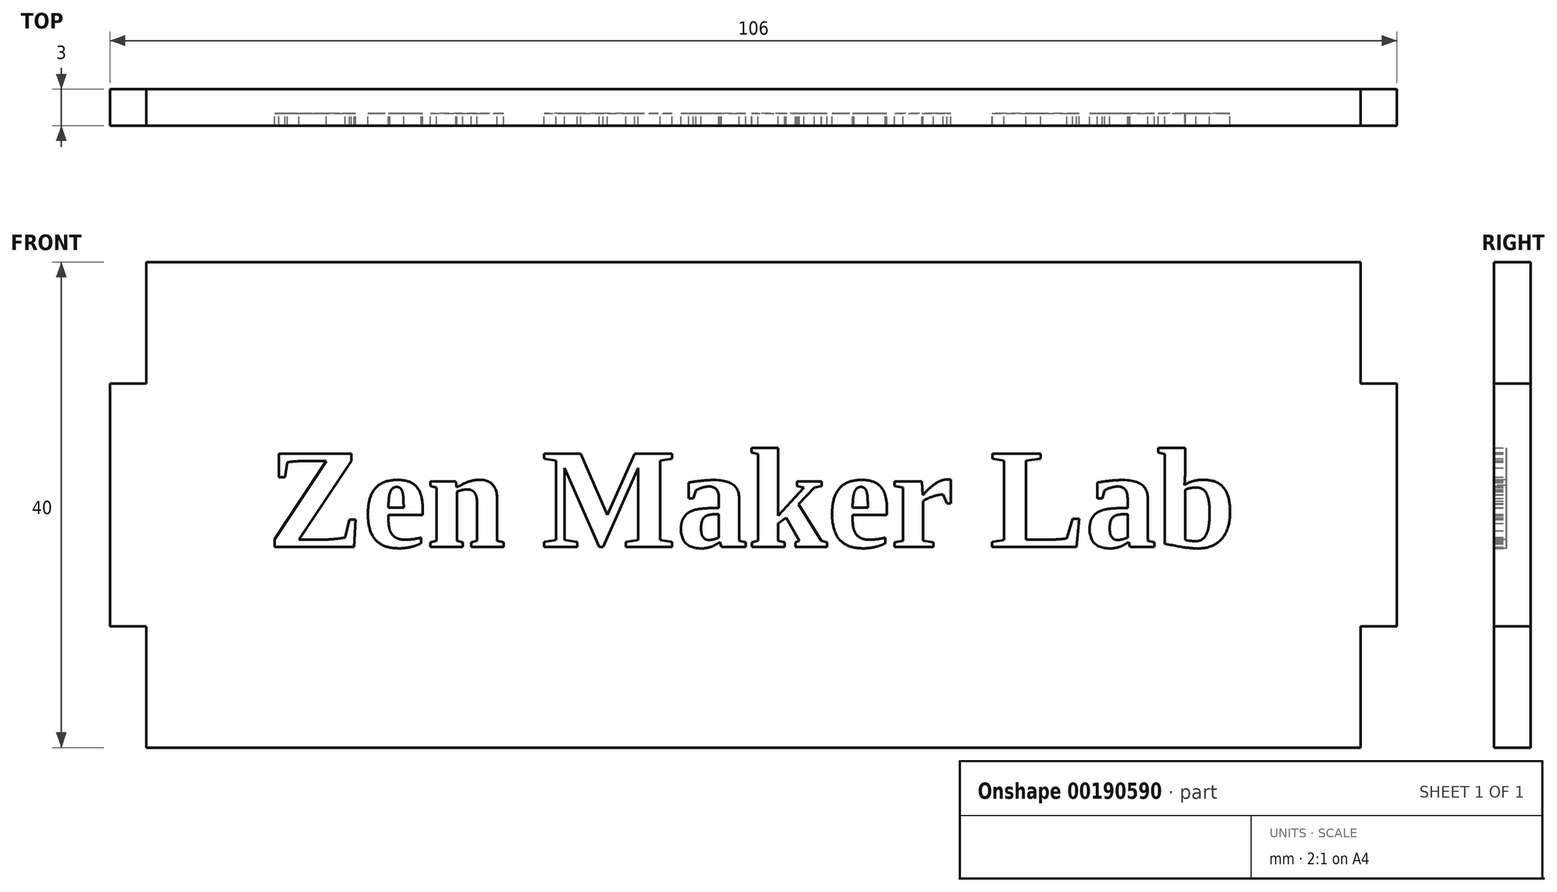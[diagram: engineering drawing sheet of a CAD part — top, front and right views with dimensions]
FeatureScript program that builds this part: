
annotation { "Feature Type Name" : "Feature", "Feature Type Description" : "" }
export const myFeature = defineFeature(function(context is Context, id is Id, definition is map)
    precondition{}
    {
        {
            var Q0;
            Q0=qCreatedBy(makeId("Front.planeOp"),FACE);
            var sketch = newSketch(context, id + "F0", { "sketchPlane" : qUnion([Q0])});
            skLineSegment(sketch, "E0.bottom", {"start": v(50, 20) * mm, "end": v(-50, 20) * mm});
            skLineSegment(sketch, "E0.top", {"start": v(50, -20) * mm, "end": v(-50, -20) * mm});
            skLineSegment(sketch, "E0.left", {"start": v(50, 20) * mm, "end": v(50, 10) * mm});
            skLineSegment(sketch, "E0.right", {"start": v(-50, 20) * mm, "end": v(-50, 10) * mm});
            skPoint(sketch, "E0.middle", {"position": v(0, 0) * mm});
            skLineSegment(sketch, "E1.bottom", {"start": v(50, 10) * mm, "end": v(53, 10) * mm});
            skLineSegment(sketch, "E1.top", {"start": v(50, -10) * mm, "end": v(53, -10) * mm});
            skLineSegment(sketch, "E1.right", {"start": v(53, 10) * mm, "end": v(53, -10) * mm});
            skLineSegment(sketch, "E2", {"start": v(0, 20) * mm, "end": v(0, -20) * mm, "construction": true});
            skLineSegment(sketch, "E3.MirrorCS", {"start": v(-50, 10) * mm, "end": v(-50, 10) * mm});
            skLineSegment(sketch, "E4.MirrorCS", {"start": v(-50, -10) * mm, "end": v(-53, -10) * mm});
            skLineSegment(sketch, "E5.MirrorCS", {"start": v(-50, 10) * mm, "end": v(-53, 10) * mm});
            skLineSegment(sketch, "E6.MirrorCS", {"start": v(-53, 10) * mm, "end": v(-53, -10) * mm});
            skLineSegment(sketch, "E7", {"start": v(-50, -10) * mm, "end": v(-50, -20) * mm});
            skLineSegment(sketch, "E8", {"start": v(50, -10) * mm, "end": v(50, -20) * mm});
            skText(sketch, "E9", { "text": "Zen Maker Lab", "fontName": "Tinos-Bold.ttf"});
            const initialGuessF0  = {"E9": [-0.04, -0.00347, 1, 0, 0.00847]};
            skSetInitialGuess(sketch, initialGuessF0);
            skSolve(sketch);
        }
        {
            var Q0;
            Q0=makeQuery(id+"F0.imprint","IMPRINT",FACE,{"disambiguationData":[TD([[makeQuery(id+"F0.imprint","IMPRINT",EDGE,{"derivedFrom":sQuery(id+"F0.wireOp",EDGE,"E0.bottom")}),1.0]])]});
            var Q1;
            Q1=makeQuery(id+"F0.imprint","IMPRINT",FACE,{"disambiguationData":[TD([[makeQuery(id+"F0.imprint","IMPRINT",EDGE,{"derivedFrom":sQuery(id+"F0.wireOp",EDGE,"E9.sketch_text.stroke-109")}),1.0]])]});
            var Q2;
            Q2=makeQuery(id+"F0.imprint","IMPRINT",FACE,{"disambiguationData":[TD([[makeQuery(id+"F0.imprint","IMPRINT",EDGE,{"derivedFrom":sQuery(id+"F0.wireOp",EDGE,"E9.sketch_text.stroke-158")}),1.0]])]});
            var Q3;
            Q3=makeQuery(id+"F0.imprint","IMPRINT",FACE,{"disambiguationData":[TD([[makeQuery(id+"F0.imprint","IMPRINT",EDGE,{"derivedFrom":sQuery(id+"F0.wireOp",EDGE,"E9.sketch_text.stroke-219")}),1.0]])]});
            var Q4;
            Q4=makeQuery(id+"F0.imprint","IMPRINT",FACE,{"disambiguationData":[TD([[makeQuery(id+"F0.imprint","IMPRINT",EDGE,{"derivedFrom":sQuery(id+"F0.wireOp",EDGE,"E9.sketch_text.stroke-226")}),1.0]])]});
            var Q5;
            Q5=makeQuery(id+"F0.imprint","IMPRINT",FACE,{"disambiguationData":[TD([[makeQuery(id+"F0.imprint","IMPRINT",EDGE,{"derivedFrom":sQuery(id+"F0.wireOp",EDGE,"E9.sketch_text.stroke-33")}),1.0]])]});
            extrude(context, id + "F1", {"entities" : qUnion([Q0, Q1, Q2, Q3, Q4, Q5]), "depth" : 3 * mm});
        }
        {
            var Q0;
            Q0=makeQuery(id+"F0.imprint","IMPRINT",FACE,{"disambiguationData":[TD([[makeQuery(id+"F0.imprint","IMPRINT",EDGE,{"derivedFrom":sQuery(id+"F0.wireOp",EDGE,"E9.sketch_text.stroke-0")}),-1.0]])]});
            var Q1;
            Q1=makeQuery(id+"F0.imprint","IMPRINT",FACE,{"disambiguationData":[TD([[makeQuery(id+"F0.imprint","IMPRINT",EDGE,{"derivedFrom":sQuery(id+"F0.wireOp",EDGE,"E9.sketch_text.stroke-17")}),-1.0]])]});
            var Q2;
            Q2=makeQuery(id+"F0.imprint","IMPRINT",FACE,{"disambiguationData":[TD([[makeQuery(id+"F0.imprint","IMPRINT",EDGE,{"derivedFrom":sQuery(id+"F0.wireOp",EDGE,"E9.sketch_text.stroke-39")}),-1.0]])]});
            var Q3;
            Q3=makeQuery(id+"F0.imprint","IMPRINT",FACE,{"disambiguationData":[TD([[makeQuery(id+"F0.imprint","IMPRINT",EDGE,{"derivedFrom":sQuery(id+"F0.wireOp",EDGE,"E9.sketch_text.stroke-63")}),-1.0]])]});
            var Q4;
            Q4=makeQuery(id+"F0.imprint","IMPRINT",FACE,{"disambiguationData":[TD([[makeQuery(id+"F0.imprint","IMPRINT",EDGE,{"derivedFrom":sQuery(id+"F0.wireOp",EDGE,"E9.sketch_text.stroke-88")}),-1.0]])]});
            var Q5;
            Q5=makeQuery(id+"F0.imprint","IMPRINT",FACE,{"disambiguationData":[TD([[makeQuery(id+"F0.imprint","IMPRINT",EDGE,{"derivedFrom":sQuery(id+"F0.wireOp",EDGE,"E9.sketch_text.stroke-116")}),-1.0]])]});
            var Q6;
            Q6=makeQuery(id+"F0.imprint","IMPRINT",FACE,{"disambiguationData":[TD([[makeQuery(id+"F0.imprint","IMPRINT",EDGE,{"derivedFrom":sQuery(id+"F0.wireOp",EDGE,"E9.sketch_text.stroke-142")}),-1.0]])]});
            var Q7;
            Q7=makeQuery(id+"F0.imprint","IMPRINT",FACE,{"disambiguationData":[TD([[makeQuery(id+"F0.imprint","IMPRINT",EDGE,{"derivedFrom":sQuery(id+"F0.wireOp",EDGE,"E9.sketch_text.stroke-164")}),-1.0]])]});
            var Q8;
            Q8=makeQuery(id+"F0.imprint","IMPRINT",FACE,{"disambiguationData":[TD([[makeQuery(id+"F0.imprint","IMPRINT",EDGE,{"derivedFrom":sQuery(id+"F0.wireOp",EDGE,"E9.sketch_text.stroke-183")}),-1.0]])]});
            var Q9;
            Q9=makeQuery(id+"F0.imprint","IMPRINT",FACE,{"disambiguationData":[TD([[makeQuery(id+"F0.imprint","IMPRINT",EDGE,{"derivedFrom":sQuery(id+"F0.wireOp",EDGE,"E9.sketch_text.stroke-198")}),-1.0]])]});
            var Q10;
            Q10=makeQuery(id+"F0.imprint","IMPRINT",FACE,{"disambiguationData":[TD([[makeQuery(id+"F0.imprint","IMPRINT",EDGE,{"derivedFrom":sQuery(id+"F0.wireOp",EDGE,"E9.sketch_text.stroke-226")}),-1.0]])]});
            extrude(context, id + "F2", {"entities" : qUnion([Q0, Q1, Q2, Q3, Q4, Q5, Q6, Q7, Q8, Q9, Q10]), "operationType" : NewBodyOperationType.ADD, "depth" : 2 * mm});
        }
    });
